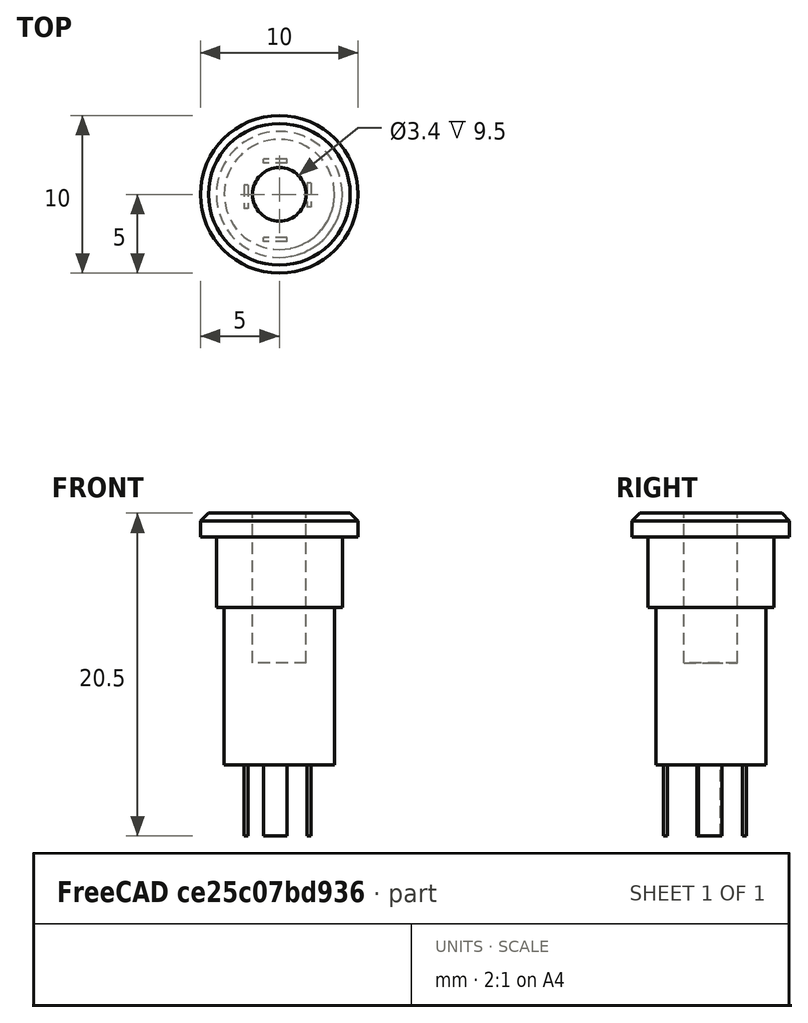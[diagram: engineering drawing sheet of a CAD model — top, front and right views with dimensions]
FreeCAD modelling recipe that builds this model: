
FCSTD DOCUMENT
Label: 3_5mm_jack_socket
License: CC-BY 3.0
LicenseURL: http://creativecommons.org/licenses/by/3.0/
objects: Part::Cylinder×4, Part::Box×4, Part::Chamfer×1, Part::MultiFuse×1, Part::Cut×1
note: 11 computed .brp shape members not serialized (recipe doc carries the construction recipe); baked Part::Feature solids carry a one-line shape summary decoded from their .brp

FEATURE [Part::Cylinder] Cylinder  label="Bezel"
  Angle = 360
  Height = 1.5
  Radius = 5
FEATURE [Part::Cylinder] Cylinder001  label="M8_threaded"
  Angle = 360
  Height = 4.6
  Placement = pos=(0,0,-4.5) rot=(0,0,1;0rad)
  Radius = 4
FEATURE [Part::Cylinder] Cylinder002
  Angle = 360
  Height = 16
  Placement = pos=(0,0,-14.5) rot=(0,0,1;0rad)
  Radius = 3.5
FEATURE [Part::Box] Box  label="Contact"
  Height = 4.6
  Length = 1.5
  Placement = pos=(-1,-3,-19) rot=(0,0,1;0rad)
  Width = 0.25
FEATURE [Part::Box] Box001  label="Contact001"
  Height = 4.6
  Length = 1.5
  Placement = pos=(-1,2,-19) rot=(0,0,1;0rad)
  Width = 0.25
FEATURE [Part::Box] Box001001  label="Contact002"
  Height = 4.6
  Length = 1.5
  Placement = pos=(2,-0.8,-19) rot=(0,0,1;1.5708rad)
  Width = 0.25
FEATURE [Part::Box] Box001002  label="Contact003"
  Height = 4.6
  Length = 1.5
  Placement = pos=(-2,-0.9,-19) rot=(0,0,1;1.5708rad)
  Width = 0.25
FEATURE [Part::Chamfer] Chamfer
  Base = -> Cylinder
  Edges = 1 edges r=0.5: [Edge1]
FEATURE [Part::Cylinder] Cylinder003  label="hole"
  Angle = 360
  Height = 10
  Placement = pos=(0,0,-8) rot=(0,0,1;0rad)
  Radius = 1.7
FEATURE [Part::MultiFuse] Fusion
  Shapes = -> [Cylinder001,Cylinder002,Box,Box001,Box001001,Box001002,Chamfer]
FEATURE [Part::Cut] Cut
  Base = -> Fusion
  Tool = -> Cylinder003
